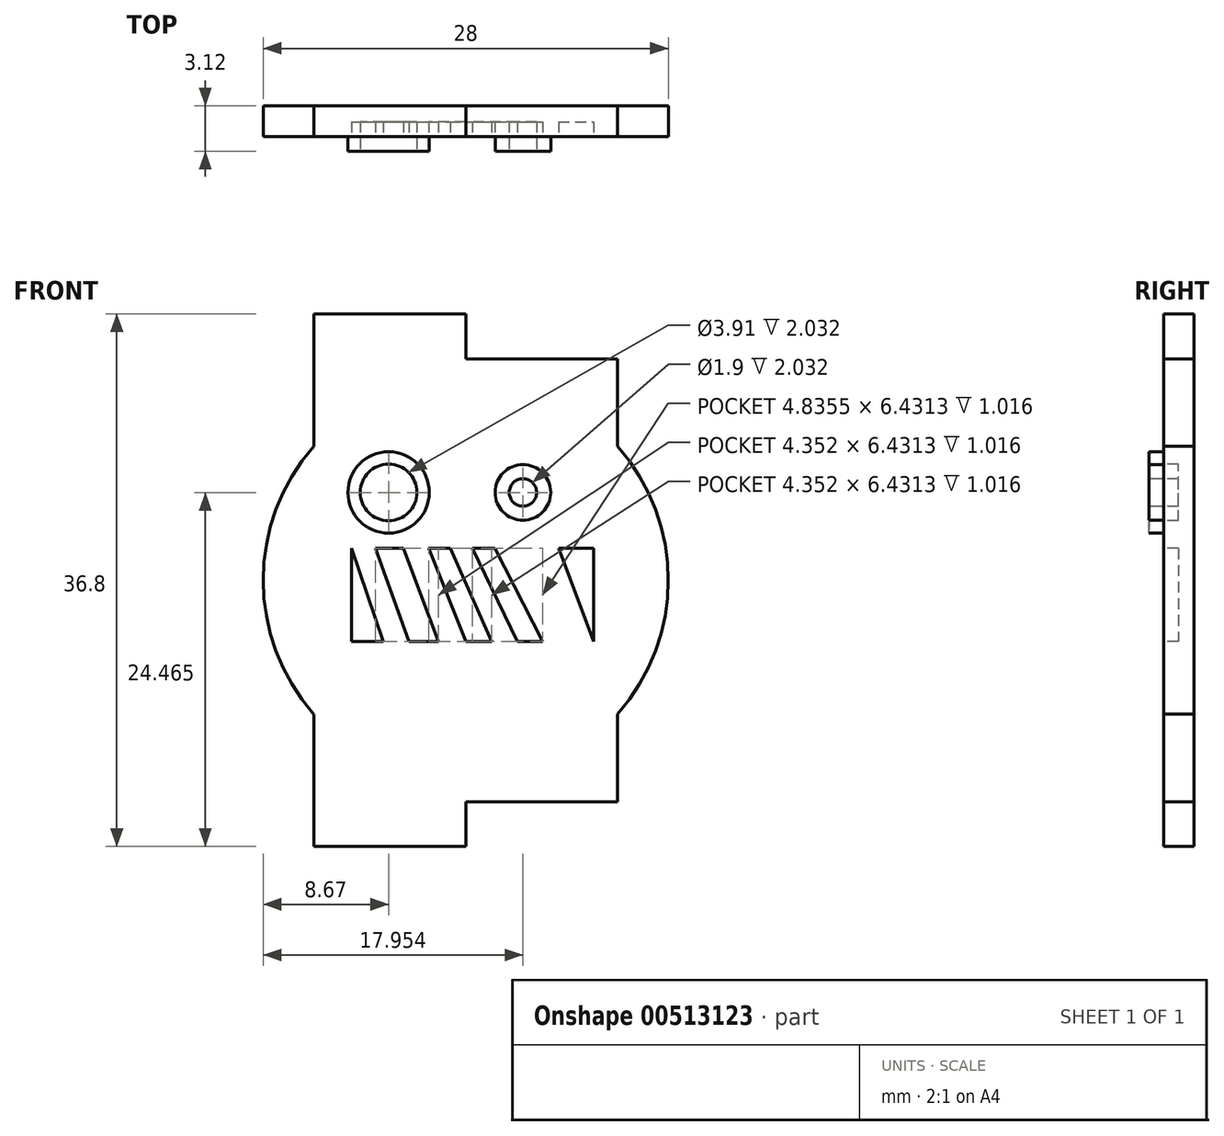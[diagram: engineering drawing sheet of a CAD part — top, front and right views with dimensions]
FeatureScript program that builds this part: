
annotation { "Feature Type Name" : "Feature", "Feature Type Description" : "" }
export const myFeature = defineFeature(function(context is Context, id is Id, definition is map)
    precondition{}
    {
        {
            var Q0;
            Q0=qCreatedBy(makeId("Front.planeOp"),FACE);
            var sketch = newSketch(context, id + "F0", { "sketchPlane" : qUnion([Q0])});
            skArc(sketch, "E0", {"start": v(-10.5, 9.27) * mm, "mid": v(-14, 0) * mm, "end": v(-10.5, -9.27) * mm});
            skLineSegment(sketch, "E1", {"start": v(0, 15.3) * mm, "end": v(10.5, 15.3) * mm});
            skLineSegment(sketch, "E2", {"start": v(10.5, 15.3) * mm, "end": v(10.5, 9.26) * mm});
            skLineSegment(sketch, "E3", {"start": v(0, 18.4) * mm, "end": v(-10.5, 18.4) * mm});
            skLineSegment(sketch, "E4", {"start": v(-10.5, 18.4) * mm, "end": v(-10.5, 9.27) * mm});
            skLineSegment(sketch, "E5", {"start": v(0, 18.4) * mm, "end": v(0, 15.3) * mm});
            skLineSegment(sketch, "E6.MirrorCS", {"start": v(0, -18.4) * mm, "end": v(-10.5, -18.4) * mm});
            skLineSegment(sketch, "E7.MirrorCS", {"start": v(0, -15.3) * mm, "end": v(10.5, -15.3) * mm});
            skLineSegment(sketch, "E8.MirrorCS", {"start": v(0, -18.4) * mm, "end": v(0, -15.3) * mm});
            skLineSegment(sketch, "E9.MirrorCS", {"start": v(-10.5, -18.4) * mm, "end": v(-10.5, -9.27) * mm});
            skLineSegment(sketch, "E10.MirrorCS", {"start": v(10.5, -15.3) * mm, "end": v(10.5, -9.26) * mm});
            skArc(sketch, "E11.trimOffspring", {"start": v(10.5, -9.26) * mm, "mid": v(14, 0) * mm, "end": v(10.5, 9.26) * mm});
            skSolve(sketch);
        }
        {
            var Q0;
            Q0=makeQuery(id+"F0.imprint","IMPRINT",FACE,{"disambiguationData":[TD([[makeQuery(id+"F0.imprint","IMPRINT",EDGE,{"derivedFrom":sQuery(id+"F0.wireOp",EDGE,"E0")}),1.0]])]});
            extrude(context, id + "F1", {"entities" : qUnion([Q0]), "depth" : 2.1 * mm});
        }
        {
            var Q0;
            Q0=makeQuery(id+"F1.opExtrude","CAP_FACE",FACE,{"disambiguationData":[OSD([sQuery(id+"F0.wireOp",EDGE,"E0"),sQuery(id+"F0.wireOp",EDGE,"E1"),sQuery(id+"F0.wireOp",EDGE,"E2"),sQuery(id+"F0.wireOp",EDGE,"E3"),sQuery(id+"F0.wireOp",EDGE,"E4"),sQuery(id+"F0.wireOp",EDGE,"E5"),sQuery(id+"F0.wireOp",EDGE,"E6.MirrorCS"),sQuery(id+"F0.wireOp",EDGE,"E7.MirrorCS"),sQuery(id+"F0.wireOp",EDGE,"E8.MirrorCS"),sQuery(id+"F0.wireOp",EDGE,"E9.MirrorCS"),sQuery(id+"F0.wireOp",EDGE,"E10.MirrorCS"),sQuery(id+"F0.wireOp",EDGE,"E11.trimOffspring")])],"isStart":false});
            var sketch = newSketch(context, id + "F2", { "sketchPlane" : qUnion([Q0])});
            skPoint(sketch, "E12.12.internal.orphan", {"position": v(0, -1.24) * mm});
            skLineSegment(sketch, "E13.bottom", {"start": v(-7.9, 2.2) * mm, "end": v(8.84, 2.2) * mm});
            skLineSegment(sketch, "E13.top", {"start": v(-7.9, -4.23) * mm, "end": v(8.84, -4.23) * mm});
            skLineSegment(sketch, "E13.left", {"start": v(-7.9, 2.2) * mm, "end": v(-7.9, -4.23) * mm});
            skLineSegment(sketch, "E13.right", {"start": v(8.84, 2.2) * mm, "end": v(8.84, -4.23) * mm});
            skCircle(sketch, "E14", {"center": v(-5.33, 6.07) * mm, "radius": 2.81 * mm});
            skLineSegment(sketch, "E15", {"start": v(-9.97, 6.07) * mm, "end": v(11.16, 6.07) * mm, "construction": true});
            skCircle(sketch, "E16", {"center": v(3.95, 6.07) * mm, "radius": 1.92 * mm});
            skCircle(sketch, "E17", {"center": v(-5.33, 6.07) * mm, "radius": 1.96 * mm});
            skCircle(sketch, "E18", {"center": v(3.95, 6.07) * mm, "radius": 0.95 * mm});
            skLineSegment(sketch, "E19", {"start": v(-7.9, 2.2) * mm, "end": v(-5.72, -4.23) * mm});
            skLineSegment(sketch, "E20", {"start": v(-5.72, -4.23) * mm, "end": v(-3.93, -4.23) * mm});
            skLineSegment(sketch, "E21", {"start": v(-3.93, -4.23) * mm, "end": v(-6.25, 2.2) * mm});
            skLineSegment(sketch, "E22", {"start": v(-6.25, 2.2) * mm, "end": v(-4.31, 2.2) * mm});
            skLineSegment(sketch, "E23", {"start": v(-4.31, 2.2) * mm, "end": v(-1.9, -4.23) * mm});
            skLineSegment(sketch, "E24", {"start": v(-1.9, -4.23) * mm, "end": v(0, -4.23) * mm});
            skLineSegment(sketch, "E25", {"start": v(0, -4.23) * mm, "end": v(-2.57, 2.2) * mm});
            skLineSegment(sketch, "E26", {"start": v(-2.57, 2.2) * mm, "end": v(-1.08, 2.2) * mm});
            skLineSegment(sketch, "E27", {"start": v(-1.08, 2.2) * mm, "end": v(1.78, -4.23) * mm});
            skLineSegment(sketch, "E28", {"start": v(1.78, -4.23) * mm, "end": v(3.57, -4.23) * mm});
            skLineSegment(sketch, "E29", {"start": v(3.57, -4.23) * mm, "end": v(0.47, 2.2) * mm});
            skLineSegment(sketch, "E30", {"start": v(0.47, 2.2) * mm, "end": v(2.02, 2.2) * mm});
            skLineSegment(sketch, "E31", {"start": v(2.02, 2.2) * mm, "end": v(5.3, -4.23) * mm});
            skLineSegment(sketch, "E32", {"start": v(5.3, -4.23) * mm, "end": v(6.42, -4.23) * mm});
            skLineSegment(sketch, "E33", {"start": v(6.42, -4.23) * mm, "end": v(3.57, 2.2) * mm});
            skLineSegment(sketch, "E34", {"start": v(3.57, 2.2) * mm, "end": v(6.42, -4.23) * mm});
            skLineSegment(sketch, "E35", {"start": v(7.63, -4.23) * mm, "end": v(5.21, 2.2) * mm});
            skLineSegment(sketch, "E36", {"start": v(8.84, -4.23) * mm, "end": v(6.42, 2.2) * mm});
            skSolve(sketch);
        }
        {
            var Q0;
            {var subQ0=sQuery(id+"F2.wireOp",EDGE,"E13.left");Q0=makeQuery(id+"F2.imprint","IMPRINT",FACE,{"disambiguationData":[TD([[makeQuery(id+"F2.imprint","IMPRINT",EDGE,{"derivedFrom":subQ0}),1.0]])]});}
            var Q1;
            {var subQ0=sQuery(id+"F2.wireOp",EDGE,"E21");Q1=makeQuery(id+"F2.imprint","IMPRINT",FACE,{"disambiguationData":[TD([[makeQuery(id+"F2.imprint","IMPRINT",EDGE,{"derivedFrom":subQ0}),-1.0]])]});}
            var Q2;
            {var subQ0=sQuery(id+"F2.wireOp",EDGE,"E25");Q2=makeQuery(id+"F2.imprint","IMPRINT",FACE,{"disambiguationData":[TD([[makeQuery(id+"F2.imprint","IMPRINT",EDGE,{"derivedFrom":subQ0}),-1.0]])]});}
            var Q3;
            {var subQ0=sQuery(id+"F2.wireOp",EDGE,"E29");Q3=makeQuery(id+"F2.imprint","IMPRINT",FACE,{"disambiguationData":[TD([[makeQuery(id+"F2.imprint","IMPRINT",EDGE,{"derivedFrom":subQ0}),-1.0]])]});}
            var Q4;
            {var subQ0=sQuery(id+"F2.wireOp",EDGE,"E34");Q4=makeQuery(id+"F2.imprint","IMPRINT",FACE,{"disambiguationData":[TD([[makeQuery(id+"F2.imprint","IMPRINT",EDGE,{"derivedFrom":subQ0}),1.0]])]});}
            var Q5;
            {var subQ0=sQuery(id+"F2.wireOp",EDGE,"E13.right");Q5=makeQuery(id+"F2.imprint","IMPRINT",FACE,{"disambiguationData":[TD([[makeQuery(id+"F2.imprint","IMPRINT",EDGE,{"derivedFrom":subQ0}),-1.0]])]});}
            var Q6;
            Q6=makeQuery(id+"F2.imprint","IMPRINT",FACE,{"disambiguationData":[TD([[makeQuery(id+"F2.imprint","IMPRINT",EDGE,{"derivedFrom":sQuery(id+"F2.wireOp",EDGE,"E17")}),1.0]])]});
            var Q7;
            Q7=makeQuery(id+"F2.imprint","IMPRINT",FACE,{"disambiguationData":[TD([[makeQuery(id+"F2.imprint","IMPRINT",EDGE,{"derivedFrom":sQuery(id+"F2.wireOp",EDGE,"E18")}),1.0]])]});
            extrude(context, id + "F3", {"entities" : qUnion([Q0, Q1, Q2, Q3, Q4, Q5, Q6, Q7]), "operationType" : NewBodyOperationType.REMOVE, "oppositeDirection" : true, "depth" : 1.02 * mm, "offsetDistance" : 25.4 * mm});
        }
        {
            var Q0;
            Q0=makeQuery(id+"F2.imprint","IMPRINT",FACE,{"disambiguationData":[TD([[makeQuery(id+"F2.imprint","IMPRINT",EDGE,{"derivedFrom":sQuery(id+"F2.wireOp",EDGE,"E14")}),1.0]])]});
            var Q1;
            Q1=makeQuery(id+"F2.imprint","IMPRINT",FACE,{"disambiguationData":[TD([[makeQuery(id+"F2.imprint","IMPRINT",EDGE,{"derivedFrom":sQuery(id+"F2.wireOp",EDGE,"E16")}),1.0]])]});
            extrude(context, id + "F4", {"entities" : qUnion([Q0, Q1]), "operationType" : NewBodyOperationType.ADD, "depth" : 1.02 * mm, "offsetDistance" : 25.4 * mm});
        }
    });
